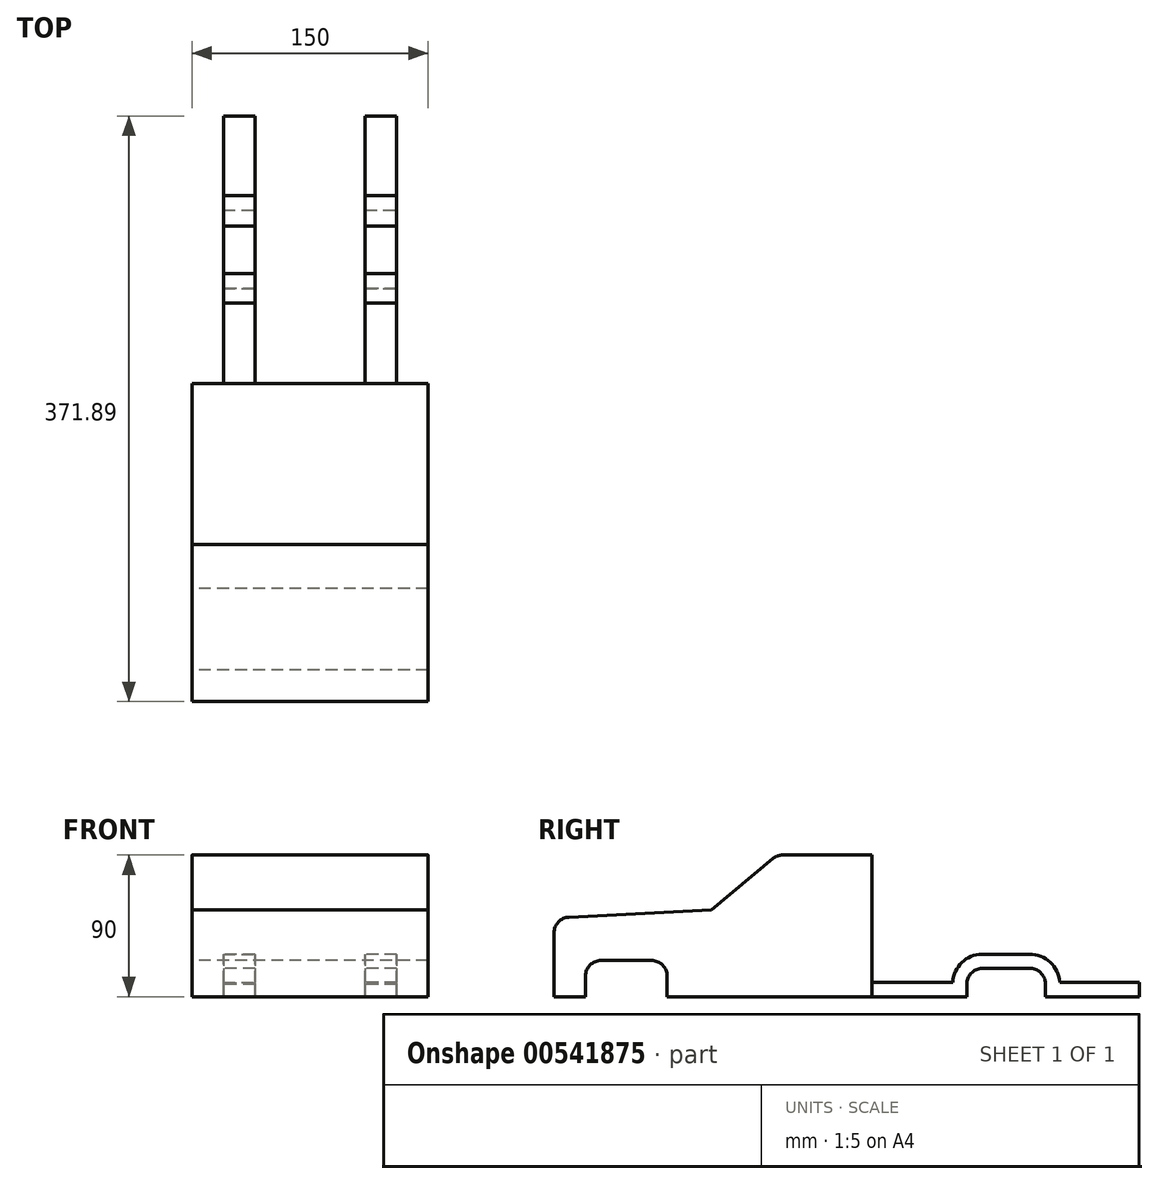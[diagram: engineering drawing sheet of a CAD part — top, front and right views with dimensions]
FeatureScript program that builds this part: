
annotation { "Feature Type Name" : "Feature", "Feature Type Description" : "" }
export const myFeature = defineFeature(function(context is Context, id is Id, definition is map)
    precondition{}
    {
        {
            var Q0;
            Q0=qCreatedBy(makeId("Right.planeOp"),FACE);
            var sketch = newSketch(context, id + "F0", { "sketchPlane" : qUnion([Q0])});
            skLineSegment(sketch, "E0", {"start": v(0, 0) * mm, "end": v(0, 40.51) * mm});
            skLineSegment(sketch, "E1", {"start": v(9.48, 50.5) * mm, "end": v(99.86, 55.23) * mm});
            skLineSegment(sketch, "E2", {"start": v(0, 0) * mm, "end": v(20, 0) * mm});
            skLineSegment(sketch, "E3", {"start": v(20, 0) * mm, "end": v(20, 13) * mm});
            skLineSegment(sketch, "E4", {"start": v(30, 23) * mm, "end": v(61.9, 23) * mm});
            skLineSegment(sketch, "E5", {"start": v(71.9, 13) * mm, "end": v(71.9, 0) * mm});
            skLineSegment(sketch, "E6", {"start": v(71.9, 0) * mm, "end": v(201.9, 0) * mm});
            skLineSegment(sketch, "E7", {"start": v(201.9, 0) * mm, "end": v(201.9, 90) * mm});
            skLineSegment(sketch, "E8", {"start": v(201.9, 90) * mm, "end": v(145.5, 90) * mm});
            skLineSegment(sketch, "E9", {"start": v(139.12, 87.7) * mm, "end": v(99.86, 55.23) * mm});
            skPoint(sketch, "E10.visualSharp", {"position": v(20, 23) * mm});
            skArc(sketch, "E10.filletArc", {"start": v(30, 23) * mm, "mid": v(22.93, 20.07) * mm, "end": v(20, 13) * mm});
            skPoint(sketch, "E11.visualSharp", {"position": v(71.9, 23) * mm});
            skArc(sketch, "E11.filletArc", {"start": v(71.9, 13) * mm, "mid": v(68.96, 20.07) * mm, "end": v(61.9, 23) * mm});
            skPoint(sketch, "E12.visualSharp", {"position": v(0, 50) * mm});
            skArc(sketch, "E12.filletArc", {"start": v(9.48, 50.5) * mm, "mid": v(2.75, 47.4) * mm, "end": v(0, 40.51) * mm});
            skPoint(sketch, "E13.visualSharp", {"position": v(141.9, 90) * mm});
            skArc(sketch, "E13.filletArc", {"start": v(145.5, 90) * mm, "mid": v(142.1, 89.4) * mm, "end": v(139.12, 87.7) * mm});
            skSolve(sketch);
        }
        {
            var Q0;
            Q0=makeQuery(id+"F0.imprint","IMPRINT",FACE,{"disambiguationData":[TD([[makeQuery(id+"F0.imprint","IMPRINT",EDGE,{"derivedFrom":sQuery(id+"F0.wireOp",EDGE,"E0")}),-1.0]])]});
            extrude(context, id + "F1", {"entities" : qUnion([Q0]), "endBound" : BoundingType.SYMMETRIC, "depth" : 150 * mm, "offsetDistance" : 25 * mm});
        }
        {
            var Q0;
            Q0=makeQuery(id+"F1.opExtrude","SWEPT_FACE",FACE,{"disambiguationData":[OSD([sQuery(id+"F0.wireOp",EDGE,"E7")])]});
            var sketch = newSketch(context, id + "F2", { "sketchPlane" : qUnion([Q0])});
            skLineSegment(sketch, "E14", {"start": v(-75, 0) * mm, "end": v(-55, 0) * mm});
            skLineSegment(sketch, "E15", {"start": v(75, 0) * mm, "end": v(55, 0) * mm});
            skLineSegment(sketch, "E16.bottom", {"start": v(-55, 0) * mm, "end": v(-35, 0) * mm});
            skLineSegment(sketch, "E16.top", {"start": v(-55, 9) * mm, "end": v(-35, 9) * mm});
            skLineSegment(sketch, "E16.left", {"start": v(-55, 0) * mm, "end": v(-55, 9) * mm});
            skLineSegment(sketch, "E16.right", {"start": v(-35, 0) * mm, "end": v(-35, 9) * mm});
            skLineSegment(sketch, "E17.bottom", {"start": v(55, 0) * mm, "end": v(35, 0) * mm});
            skLineSegment(sketch, "E17.top", {"start": v(55, 9) * mm, "end": v(35, 9) * mm});
            skLineSegment(sketch, "E17.left", {"start": v(55, 0) * mm, "end": v(55, 9) * mm});
            skLineSegment(sketch, "E17.right", {"start": v(35, 0) * mm, "end": v(35, 9) * mm});
            skSolve(sketch);
        }
        {
            var Q0;
            Q0=qCreatedBy(makeId("Right.planeOp"),FACE);
            var sketch = newSketch(context, id + "F3", { "sketchPlane" : qUnion([Q0])});
            skLineSegment(sketch, "E18", {"start": v(202.2, 0) * mm, "end": v(262.2, 0) * mm});
            skLineSegment(sketch, "E19", {"start": v(262.2, 0) * mm, "end": v(262.2, 8) * mm});
            skLineSegment(sketch, "E20", {"start": v(272.2, 18) * mm, "end": v(302.2, 18) * mm});
            skLineSegment(sketch, "E21", {"start": v(312.2, 8) * mm, "end": v(312.2, 0) * mm});
            skLineSegment(sketch, "E22", {"start": v(312.2, 0) * mm, "end": v(372.2, 0) * mm});
            skPoint(sketch, "E23.visualSharp", {"position": v(262.2, 18) * mm});
            skArc(sketch, "E23.filletArc", {"start": v(272.2, 18) * mm, "mid": v(265.13, 15.07) * mm, "end": v(262.2, 8) * mm});
            skPoint(sketch, "E24.visualSharp", {"position": v(312.2, 18) * mm});
            skArc(sketch, "E24.filletArc", {"start": v(312.2, 8) * mm, "mid": v(309.27, 15.07) * mm, "end": v(302.2, 18) * mm});
            skSolve(sketch);
        }
        {
            var Q0;
            Q0=makeQuery(id+"F2.imprint","IMPRINT",FACE,{"disambiguationData":[TD([[makeQuery(id+"F2.imprint","IMPRINT",EDGE,{"derivedFrom":sQuery(id+"F2.wireOp",EDGE,"E16.bottom")}),1.0]])]});
            var Q1;
            Q1=makeQuery(id+"F2.imprint","IMPRINT",FACE,{"disambiguationData":[TD([[makeQuery(id+"F2.imprint","IMPRINT",EDGE,{"derivedFrom":sQuery(id+"F2.wireOp",EDGE,"E17.bottom")}),1.0]])]});
            var Q2;
            Q2=sQuery(id+"F3.wireOp",EDGE,"E18");
            var Q3;
            Q3=sQuery(id+"F3.wireOp",EDGE,"E19");
            var Q4;
            Q4=sQuery(id+"F3.wireOp",EDGE,"E20");
            var Q5;
            Q5=sQuery(id+"F3.wireOp",EDGE,"E22");
            var Q6;
            Q6=sQuery(id+"F3.wireOp",EDGE,"E21");
            var Q7;
            Q7=sQuery(id+"F3.wireOp",EDGE,"E23.filletArc");
            var Q8;
            Q8=sQuery(id+"F3.wireOp",EDGE,"E24.filletArc");
            sweep(context, id + "F4", {"operationType" : NewBodyOperationType.ADD, "profiles" : qUnion([Q0, Q1]), "path" : qUnion([Q2, Q3, Q4, Q5, Q6, Q7, Q8])});
        }
    });
